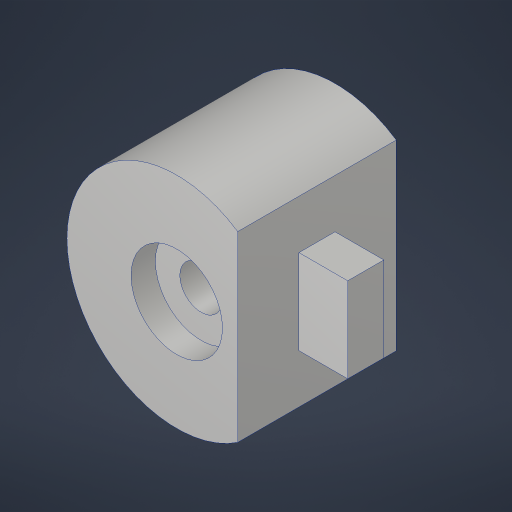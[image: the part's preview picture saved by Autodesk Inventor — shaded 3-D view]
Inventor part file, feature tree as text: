
AUTODESK INVENTOR PART (.ipt)
format: ipt  version: 2023.4 (Build 274418000, 418)  size: 210,432 bytes
history: native  units: in
note: dims shown in document units (in); Inventor stores cm internally (conversion verified against a paired STEP export)
features: extrude x4, sketch x4, projected_geometry x1
ambient origin geometry x8: Origin, YZ Plane, XZ Plane, XY Plane, X Axis, Y Axis, Z Axis, Center Point
bodies: Solid1 (feature_tree)
feature tree (9):
  extrude  "Extrusion1"  Depth=4.5in
  extrude  "Extrusion2"  Depth=0.25in
  extrude  "Extrusion3"  Depth=0.8358in
  extrude  "Extrusion5"  Depth=3.25in TaperAngle=0.0deg
  sketch  "Sketch1"  dims[d0=0.875in d2=4.5in]
  sketch  "Sketch3"  dims[d3=3.5in d4=0.25in]
  sketch  "Sketch4"  dims[d5=1.4142in d6=0.8358in]
  sketch  "Sketch7"  dims[d7=1.25in d8=3.25in d9=0.0in d10=1.875in d11=0.5in d12=0.0in d13=1.875in d14=0.5in d15=0.0in d34=1.0in d35=2.0in d36=0.125in d37=0.125in d38=0.005in d39=0.005in d40=1.0in d41=0.0in]
  projected_geometry  "Project Cut Edges1"
